# Revit family: LAMP_FIL 70 TECH ASYM SUSPENDED DALI
name_source: partatom
category: Luminarias
revit_build: Autodesk Revit 2015 (Build: 20140606_1530(x64)
units: mm (PartAtom-declared; Revit-internal decimal feet)

## types (16) — shared parameters
CRI = 80
Cambio de temperatura de color de luz atenuada = <Ninguno>
Comentarios de tipo = Availability of switching between accessories through visibility parameters when placed in a project.
Fabricante = LAMP
Filtro de color = 16777215
Gear = Adjustable DALI
IEE = A+
IFC Clasificación = Light Fixture
Installation instructions = https://www.lamp.es
Insulation class = I
LED Lifetime = 50.000 L80 B10
Last update = 17/08/2020
Luminaire type = Indoor - Modular System
Lámpara = MID POWER LED
MacAdam = 3
Manufacturer URL = http://www.lamp.es
Manufacturer country = Spain
Manufacturer name = LAMP
Material Reflector = LAMP_PC Reflector Fil Tech Metalizado
Model explanation = Availability of switching between accessories through visibility parameters when placed in a project.
Power Supply = 220-240V 50-60Hz
Product URL = https://www.lamp.es
Product datasheet = https://www.lamp.es
Protection rating = IP20
Type = MID POWER NICHIA
UGR = 19
Ángulo de inclinación = 90,00°

## per-type parameters (varying)
| type | Archivo de red fotométrica | Descripción | Dimensions | Efficacy | Finish | Largo | Material Perfil | Modelo | Plum | Power | Product code | UniClass 1.4 Code | UniClass 2.0 Code | Weight |
| 1000MM 1600LM 3000K WHITE | 14741200.IES | FIL 70 TECH ASYM SUS 1M 1600 WW DALI WH. | 1000 x 70 x 70 mm | 96 lm/W | Matt white | 1000 mm  [stored 3.28084 ft] | LAMP_Aluminio Perfil Fil BL | F71SF100LOTA830DW | 15 W | 12 W | F71SF100LOTA830DW | F71SF100LOTA830DW | F71SF100LOTA830DW | 2,39 kg |
| 1000MM 1600LM 3000K GREY | 14741203.IES | FIL 70 TECH ASYM SUS 1M 1600 WW DALI GR. | 1000 x 70 x 70 mm | 96 lm/W | Gloss grey | 1000 mm  [stored 3.28084 ft] | LAMP_Aluminio Perfil Fil GR | F71SF100LOTA830DG | 15 W | 12 W | F71SF100LOTA830DG | F71SF100LOTA830DG | F71SF100LOTA830DG | 2,39 kg |
| 1000MM 1600LM 4000K WHITE | 14740200.IES | FIL 70 TECH ASYM SUS 1M 1600 NW DALI WH. | 1000 x 70 x 70 mm | 96 lm/W | Matt white | 1000 mm  [stored 3.28084 ft] | LAMP_Aluminio Perfil Fil BL | F71SF100LOTA840DW | 15 W | 12 W | F71SF100LOTA840DW | F71SF100LOTA840DW | F71SF100LOTA840DW | 2,39 kg |
| 1000MM 1600LM 4000K GREY | 14740203.IES | FIL + LED TECH ASYM SUS 1M 1600 NW DALI GR. | 1000 x 70 x 70 mm | 96 lm/W | Gloss grey | 1000 mm  [stored 3.28084 ft] | LAMP_Aluminio Perfil Fil GR | F71SF100LOTA840DG | 15 W | 12 W | F71SF100LOTA840DG | F71SF100LOTA840DG | F71SF100LOTA840DG | 2,39 kg |
| 1000MM 3200LM 3000K WHITE | 14741210.IES | FIL + LED TECH ASYM SUS 1M 3200 WW DALI WH. | 1000 x 70 x 70 mm | 86 lm/W | Matt white | 1000 mm  [stored 3.28084 ft] | LAMP_Aluminio Perfil Fil BL | F71SF100MOTA830DW | 24 W | 21 W | F71SF100MOTA830DW | F71SF100MOTA830DW | F71SF100MOTA830DW | 2,39 kg |
| 1000MM 3200LM 3000K GREY | 14741213.IES | FIL 70 TECH ASYM SUS 1M 3200 WW DALI GR. | 1000 x 70 x 70 mm | 86 lm/W | Gloss grey | 1000 mm  [stored 3.28084 ft] | LAMP_Aluminio Perfil Fil GR | F71SF100MOTA830DG | 24 W | 21 W | F71SF100MOTA830DG | F71SF100MOTA830DG | F71SF100MOTA830DG | 2,39 kg |
| 1000MM 3200LM 4000K WHITE | 14740210.IES | FIL + LED TECH ASYM SUS 1M 3200 NW DALI WH. | 1000 x 70 x 70 mm | 86 lm/W | Matt white | 1000 mm  [stored 3.28084 ft] | LAMP_Aluminio Perfil Fil BL | F71SF100MOTA840DW | 24 W | 21 W | F71SF100MOTA840DW | F71SF100MOTA840DW | F71SF100MOTA840DW | 2,39 kg |
| 1000MM 3200LM 4000K GREY | 14740213.IES | FIL 70 TECH ASYM SUS 1M 3200 NW DALI GR. | 1000 x 70 x 70 mm | 86 lm/W | Gloss grey | 1000 mm  [stored 3.28084 ft] | LAMP_Aluminio Perfil Fil GR | F71SF100MOTA840DG | 24 W | 21 W | F71SF100MOTA840DG | F71SF100MOTA840DG | F71SF100MOTA840DG | 2,39 kg |
| 2000MM 3200LM 3000K WHITE | 14741220.IES | FIL 70 TECH ASYM SUS 2M 3200 WW DALI WH. | 2000 x 70 x 70 mm | 104 lm/W | Matt white | 2000 mm  [stored 6.56168 ft] | LAMP_Aluminio Perfil Fil BL | F71SF200MOTA830DW | 27 W | 25 W | F71SF200MOTA830DW | F71SF200MOTA830DW | F71SF200MOTA830DW | 4,62 kg |
| 2000MM 3200LM 3000K GREY | 14741223.IES | FIL 70 TECH ASYM SUS 2M 3200 WW DALI GR. | 2000 x 70 x 70 mm | 104 lm/W | Gloss grey | 2000 mm  [stored 6.56168 ft] | LAMP_Aluminio Perfil Fil GR | F71SF200MOTA830DG | 27 W | 25 W | F71SF200MOTA830DG | F71SF200MOTA830DG | F71SF200MOTA830DG | 4,62 kg |
| 2000MM 3200LM 4000K WHITE | 14740220.IES | FIL 70 TECH ASYM SUS 2M 3200 NW DALI WH. | 2000 x 70 x 70 mm | 104 lm/W | Matt white | 2000 mm  [stored 6.56168 ft] | LAMP_Aluminio Perfil Fil BL | F71SF200MOTA840DW | 27 W | 25 W | F71SF200MOTA840DW | F71SF200MOTA840DW | F71SF200MOTA840DW | 4,62 kg |
| 2000MM 3200LM 4000K GREY | 14740223.IES | FIL 70 TECH ASYM SUS 2M 3200 NW DALI GR. | 2000 x 70 x 70 mm | 104 lm/W | Gloss grey | 2000 mm  [stored 6.56168 ft] | LAMP_Aluminio Perfil Fil GR | F71SF200MOTA840DG | 27 W | 25 W | F71SF200MOTA840DG | F71SF200MOTA840DG | F71SF200MOTA840DG | 4,62 kg |
| 2000MM 6400LM 3000K WHITE | 14741230.IES | FIL 70 TECH ASYM SUS 2M 6400 WW DALI WH. | 2000 x 70 x 70 mm | 91 lm/W | Matt white | 2000 mm  [stored 6.56168 ft] | LAMP_Aluminio Perfil Fil BL | F71SF200HOTA830DW | 45 W | 42 W | F71SF200HOTA830DW | F71SF200HOTA830DW | F71SF200HOTA830DW | 4,62 kg |
| 2000MM 6400LM 3000K GREY | 14741233.IES | FIL 70 TECH ASYM SUS 2M 6400 WW DALI GR. | 2000 x 70 x 70 mm | 91 lm/W | Gloss grey | 2000 mm  [stored 6.56168 ft] | LAMP_Aluminio Perfil Fil GR | F71SF200HOTA830DG | 45 W | 42 W | F71SF200HOTA830DG | F71SF200HOTA830DG | F71SF200HOTA830DG | 4,62 kg |
| 2000MM 6400LM 4000K WHITE | 14740230.IES | FIL 70 TECH ASYM SUS 2M 6400 NW DALI WH. | 2000 x 70 x 70 mm | 91 lm/W | Matt white | 2000 mm  [stored 6.56168 ft] | LAMP_Aluminio Perfil Fil BL | F71SF200HOTA840DW | 45 W | 42 W | F71SF200HOTA840DW | F71SF200HOTA840DW | F71SF200HOTA840DW | 4,62 kg |
| 2000MM 6400LM 4000K GREY | 14740233.IES | FIL 70 TECH ASYM SUS 2M 6400 NW DALI GR. | 2000 x 70 x 70 mm | 91 lm/W | Gloss grey | 2000 mm  [stored 6.56168 ft] | LAMP_Aluminio Perfil Fil GR | F71SF200HOTA840DG | 45 W | 42 W | F71SF200HOTA840DG | F71SF200HOTA840DG | F71SF200HOTA840DG | 4,62 kg |

note: [stored X ft] marks values corroborated as IEEE doubles in the binary element streams (Revit-internal decimal feet)

## geometry (parser evidence)
native form markers: Blend x10
no freeform markers — native parametric forms only
